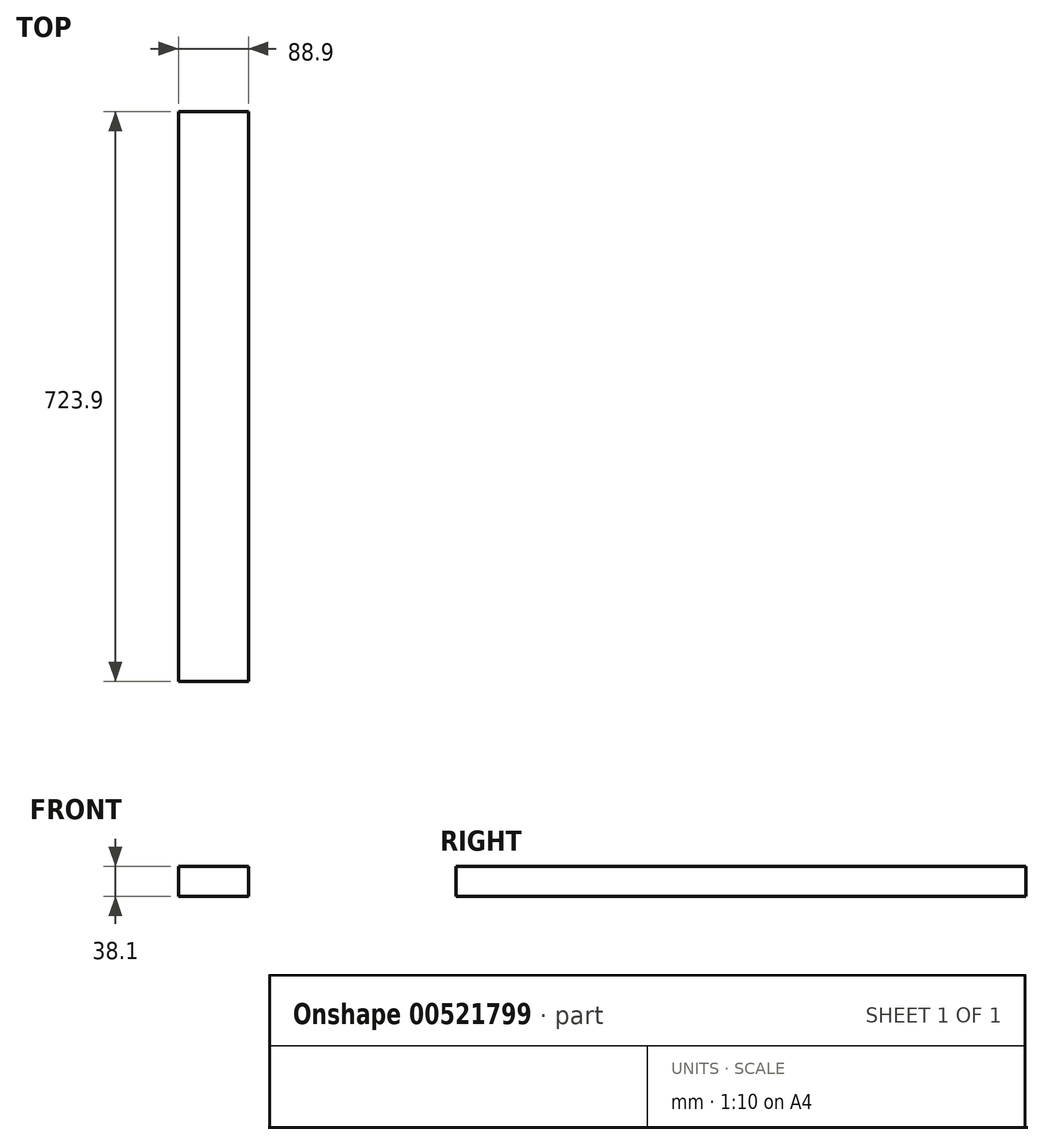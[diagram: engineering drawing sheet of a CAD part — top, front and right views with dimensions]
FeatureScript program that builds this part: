
annotation { "Feature Type Name" : "Feature", "Feature Type Description" : "" }
export const myFeature = defineFeature(function(context is Context, id is Id, definition is map)
    precondition{}
    {
        {
            var Q0;
            Q0=qCreatedBy(makeId("Front.planeOp"),FACE);
            var sketch = newSketch(context, id + "F0", { "sketchPlane" : qUnion([Q0])});
            skLineSegment(sketch, "E0.bottom", {"start": v(0, 0) * mm, "end": v(88.9, 0) * mm});
            skLineSegment(sketch, "E0.top", {"start": v(0, 38.1) * mm, "end": v(88.9, 38.1) * mm});
            skLineSegment(sketch, "E0.left", {"start": v(0, 0) * mm, "end": v(0, 38.1) * mm});
            skLineSegment(sketch, "E0.right", {"start": v(88.9, 0) * mm, "end": v(88.9, 38.1) * mm});
            skSolve(sketch);
        }
        {
            var Q0;
            Q0 = qSketchRegion(id + "F0", true);
            extrude(context, id + "F1", {"entities" : qUnion([Q0]), "oppositeDirection" : true, "depth" : 723.9 * mm, "offsetDistance" : 25.4 * mm});
        }
    });
